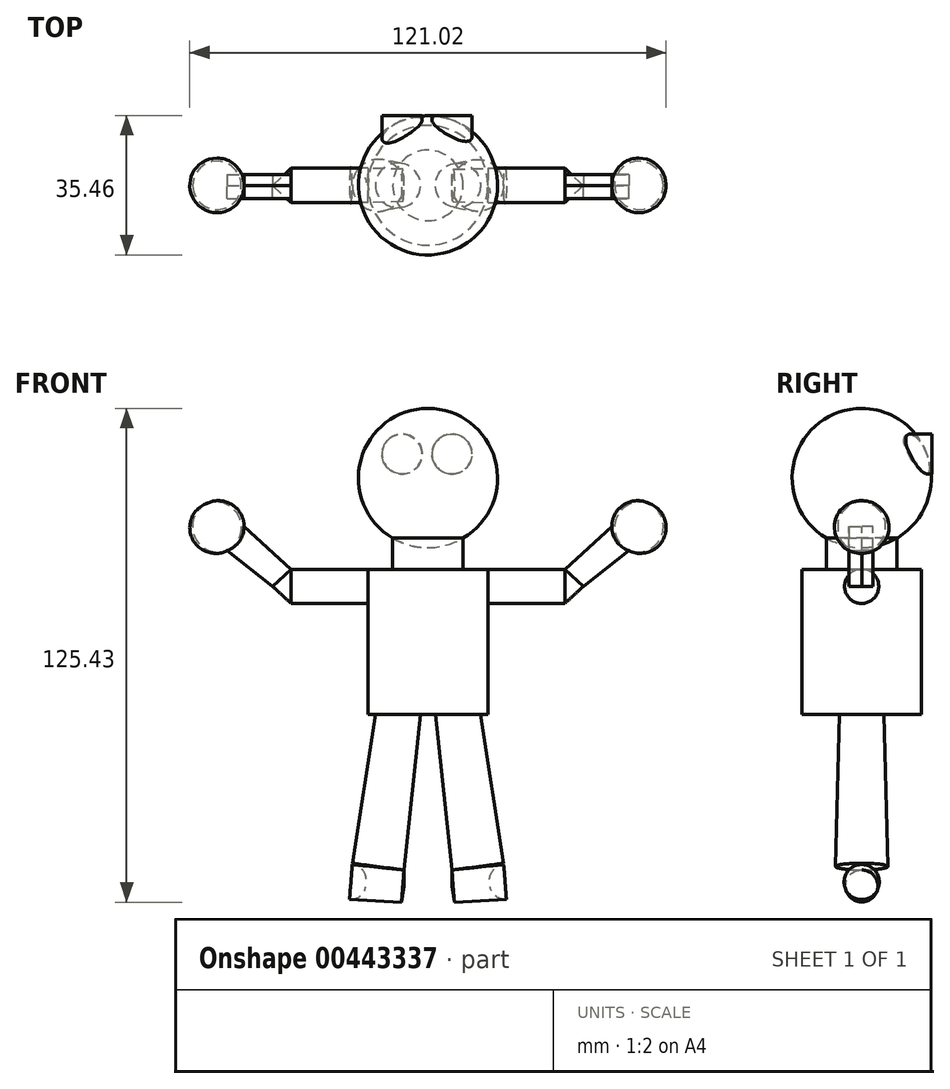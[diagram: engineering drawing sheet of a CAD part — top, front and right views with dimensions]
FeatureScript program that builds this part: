
annotation { "Feature Type Name" : "Feature", "Feature Type Description" : "" }
export const myFeature = defineFeature(function(context is Context, id is Id, definition is map)
    precondition{}
    {
        {
            var Q0;
            Q0=qCreatedBy(makeId("Front.planeOp"),FACE);
            var sketch = newSketch(context, id + "F0", { "sketchPlane" : qUnion([Q0])});
            skCircle(sketch, "E0", {"center": v(0, 44.17) * mm, "radius": 17.68 * mm});
            skLineSegment(sketch, "E1", {"start": v(-8.95, 28.92) * mm, "end": v(-8.95, 21) * mm});
            skLineSegment(sketch, "E2", {"start": v(-8.95, 21) * mm, "end": v(-22.45, 21) * mm});
            skLineSegment(sketch, "E3", {"start": v(-34.76, 21) * mm, "end": v(-46.7, 31.86) * mm});
            skLineSegment(sketch, "E4", {"start": v(0, 61.85) * mm, "end": v(0, 26.49) * mm});
            skLineSegment(sketch, "E5", {"start": v(-34.76, 21) * mm, "end": v(-22.45, 21) * mm});
            skCircle(sketch, "E6", {"center": v(-53.25, 31.87) * mm, "radius": 6.55 * mm});
            skPoint(sketch, "E6.second.point", {"position": v(-59.8, 31.86) * mm});
            skPoint(sketch, "E6.third.point", {"position": v(-56.16, 37.74) * mm});
            skLineSegment(sketch, "E7", {"start": v(-56.16, 37.74) * mm, "end": v(-51.05, 25.7) * mm});
            skLineSegment(sketch, "E8", {"start": v(-51.05, 25.7) * mm, "end": v(-39.46, 16.65) * mm});
            skLineSegment(sketch, "E9", {"start": v(-39.46, 16.65) * mm, "end": v(-33.78, 13.48) * mm});
            skLineSegment(sketch, "E10", {"start": v(-33.78, 13.48) * mm, "end": v(-15.2, 13.48) * mm});
            skLineSegment(sketch, "E11", {"start": v(-15.2, 13.48) * mm, "end": v(-15.2, -15.93) * mm});
            skLineSegment(sketch, "E12", {"start": v(-15.2, -15.93) * mm, "end": v(0, -15.93) * mm});
            skLineSegment(sketch, "E13", {"start": v(0, -15.93) * mm, "end": v(0, 61.85) * mm});
            skLineSegment(sketch, "E14", {"start": v(-8.95, 21) * mm, "end": v(0, 21) * mm});
            skLineSegment(sketch, "E15", {"start": v(-15.2, 13.48) * mm, "end": v(-15.2, 21) * mm});
            skLineSegment(sketch, "E16", {"start": v(-39.46, 16.65) * mm, "end": v(-15.2, 16.65) * mm});
            skLineSegment(sketch, "E17", {"start": v(-39.46, 16.65) * mm, "end": v(-34.76, 21) * mm});
            skCircle(sketch, "E18.MirrorC", {"center": v(53.25, 31.87) * mm, "radius": 6.55 * mm});
            skLineSegment(sketch, "E19.MirrorCS", {"start": v(34.76, 21) * mm, "end": v(46.7, 31.86) * mm});
            skLineSegment(sketch, "E20.MirrorCS", {"start": v(51.05, 25.7) * mm, "end": v(39.46, 16.65) * mm});
            skLineSegment(sketch, "E21.MirrorCS", {"start": v(39.46, 16.65) * mm, "end": v(34.76, 21) * mm});
            skLineSegment(sketch, "E22.MirrorCS", {"start": v(33.78, 13.48) * mm, "end": v(15.2, 13.48) * mm});
            skLineSegment(sketch, "E23.MirrorCS", {"start": v(39.46, 16.65) * mm, "end": v(15.2, 16.65) * mm});
            skLineSegment(sketch, "E24.MirrorCS", {"start": v(56.16, 37.74) * mm, "end": v(51.05, 25.7) * mm});
            skLineSegment(sketch, "E25", {"start": v(-12.66, -54.7) * mm, "end": v(-6.08, -55.4) * mm});
            skLineSegment(sketch, "E26", {"start": v(-6.08, -55.4) * mm, "end": v(-1.9, -15.93) * mm});
            skPoint(sketch, "E27.end.orphan", {"position": v(-12.66, -54.7) * mm});
            skPoint(sketch, "E27.start.orphan", {"position": v(-7.6, -15.93) * mm});
            skLineSegment(sketch, "E28", {"start": v(-7.6, -15.93) * mm, "end": v(-12.66, -54.7) * mm});
            skPoint(sketch, "E29.orphan", {"position": v(-19.24, -54) * mm});
            skPoint(sketch, "E30.start.orphan", {"position": v(-16.5, -58.16) * mm});
            skPoint(sketch, "E31.start.orphan", {"position": v(-6.08, -59.52) * mm});
            skPoint(sketch, "E32.end.orphan", {"position": v(-12.66, -61.61) * mm});
            skLineSegment(sketch, "E33", {"start": v(-12.66, -54.7) * mm, "end": v(-19.24, -54) * mm});
            skArc(sketch, "E34", {"start": v(-19.24, -54) * mm, "mid": v(-23.66, -58) * mm, "end": v(-19.24, -61.97) * mm});
            skLineSegment(sketch, "E35", {"start": v(-23.66, -58.16) * mm, "end": v(-6.08, -59.52) * mm});
            skLineSegment(sketch, "E36", {"start": v(-6.08, -59.52) * mm, "end": v(-6.08, -55.4) * mm});
            skSolve(sketch);
        }
        {
            var Q0;
            {var subQ0=sQuery(id+"F0.wireOp",EDGE,"E0");var subQ1=makeQuery(id+"F0.imprint","INTERSECT",VERTEX,{"derivedFrom":[subQ0,sQuery(id+"F0.wireOp",EDGE,"E1")]});Q0=makeQuery(id+"F0.imprint","IMPRINT",FACE,{"disambiguationData":[TD([[makeQuery(id+"F0.imprint","IMPRINT",EDGE,{"disambiguationData":[TD([[subQ1,1.0]])],"derivedFrom":subQ0}),1.0]])]});}
            var Q1;
            Q1=sQuery(id+"F0.wireOp",EDGE,"E4");
            revolve(context, id + "F1", {"entities" : qUnion([Q0]), "axis" : qUnion([Q1]), "revolveType" : RevolveType.FULL});
        }
        {
            var Q0;
            {var subQ0=sQuery(id+"F0.wireOp",EDGE,"E7");Q0=makeQuery(id+"F0.imprint","IMPRINT",FACE,{"disambiguationData":[TD([[makeQuery(id+"F0.imprint","IMPRINT",EDGE,{"derivedFrom":subQ0}),-1.0]])]});}
            var Q1;
            Q1=sQuery(id+"F0.wireOp",EDGE,"E7");
            revolve(context, id + "F2", {"entities" : qUnion([Q0]), "axis" : qUnion([Q1]), "revolveType" : RevolveType.FULL});
        }
        {
            var Q0;
            {var subQ3=sQuery(id+"F0.wireOp",EDGE,"E11");Q0=makeQuery(id+"F0.imprint","IMPRINT",FACE,{"disambiguationData":[TD([[makeQuery(id+"F0.imprint","IMPRINT",EDGE,{"derivedFrom":subQ3}),1.0]])]});}
            var Q1;
            Q1=sQuery(id+"F0.wireOp",EDGE,"E13");
            revolve(context, id + "F3", {"entities" : qUnion([Q0]), "axis" : qUnion([Q1]), "revolveType" : RevolveType.FULL});
        }
        {
            var Q0;
            {var subQ3=sQuery(id+"F0.wireOp",EDGE,"E16");Q0=makeQuery(id+"F0.imprint","IMPRINT",FACE,{"disambiguationData":[TD([[makeQuery(id+"F0.imprint","IMPRINT",EDGE,{"derivedFrom":subQ3}),1.0]])]});}
            var Q1;
            Q1=sQuery(id+"F0.wireOp",EDGE,"E16");
            revolve(context, id + "F4", {"entities" : qUnion([Q0]), "axis" : qUnion([Q1]), "revolveType" : RevolveType.FULL});
        }
        {
            var Q0;
            {var subQ0=sQuery(id+"F0.wireOp",EDGE,"E1");Q0=makeQuery(id+"F0.imprint","IMPRINT",FACE,{"disambiguationData":[TD([[makeQuery(id+"F0.imprint","IMPRINT",EDGE,{"derivedFrom":subQ0}),1.0]])]});}
            var Q1;
            Q1=sQuery(id+"F0.wireOp",EDGE,"E13");
            revolve(context, id + "F5", {"entities" : qUnion([Q0]), "axis" : qUnion([Q1]), "revolveType" : RevolveType.FULL});
        }
        {
            var Q0;
            Q0=makeQuery(id+"FW3MMF7VYioO6fB_0.opRevolve","SWEPT_BODY",BODY,{"disambiguationData":[OSD([sQuery(id+"F0.wireOp",EDGE,"zyPNzYHr-ha5P-rXSg-KlId-yvSlWLOifB84"),sQuery(id+"F0.wireOp",EDGE,"ewyTBzqX-5RmW-i4Gw-5EuK-rlDggEhh6qsi"),sQuery(id+"F0.wireOp",EDGE,"E5"),sQuery(id+"F0.wireOp",EDGE,"1kdRDDVu-V9N2-t5Jb-sepC-QsSfjgobqoIw")])]});
            var Q1;
            Q1=makeQuery(id+"F2.opRevolve","SWEPT_BODY",BODY,{"disambiguationData":[OSD([sQuery(id+"F0.wireOp",EDGE,"E6"),sQuery(id+"F0.wireOp",EDGE,"E7")])]});
            var Q2;
            Q2=makeQuery(id+"F4.opRevolve","SWEPT_BODY",BODY,{"disambiguationData":[OSD([sQuery(id+"F0.wireOp",EDGE,"E2"),sQuery(id+"F0.wireOp",EDGE,"E5"),sQuery(id+"F0.wireOp",EDGE,"E15"),sQuery(id+"F0.wireOp",EDGE,"E16"),sQuery(id+"F0.wireOp",EDGE,"E17")])]});
            var Q3;
            Q3=qCreatedBy(makeId("Right.planeOp"),FACE);
            mirror(context, id + "F6", {"entities" : qUnion([Q0, Q1, Q2]), "mirrorPlane" : qUnion([Q3])});
        }
        {
            var Q0;
            {var subQ0=sQuery(id+"F0.wireOp",EDGE,"E3");Q0=makeQuery(id+"F0.imprint","IMPRINT",FACE,{"disambiguationData":[TD([[makeQuery(id+"F0.imprint","IMPRINT",EDGE,{"derivedFrom":subQ0}),1.0]])]});}
            var Q1;
            {var subQ0=sQuery(id+"F0.wireOp",EDGE,"E19.MirrorCS");Q1=makeQuery(id+"F0.imprint","IMPRINT",FACE,{"disambiguationData":[TD([[makeQuery(id+"F0.imprint","IMPRINT",EDGE,{"derivedFrom":subQ0}),-1.0]])]});}
            extrude(context, id + "F7", {"entities" : qUnion([Q0, Q1]), "oppositeDirection" : true, "depth" : 2.8 * mm});
        }
        {
            var Q0;
            {var subQ0=sQuery(id+"F0.wireOp",EDGE,"E19.MirrorCS");Q0=makeQuery(id+"F0.imprint","IMPRINT",FACE,{"disambiguationData":[TD([[makeQuery(id+"F0.imprint","IMPRINT",EDGE,{"derivedFrom":subQ0}),-1.0]])]});}
            var Q1;
            {var subQ0=sQuery(id+"F0.wireOp",EDGE,"E3");Q1=makeQuery(id+"F0.imprint","IMPRINT",FACE,{"disambiguationData":[TD([[makeQuery(id+"F0.imprint","IMPRINT",EDGE,{"derivedFrom":subQ0}),1.0]])]});}
            extrude(context, id + "F8", {"entities" : qUnion([Q0, Q1]), "depth" : 3.3 * mm});
        }
        {
            var Q0;
            {var subQ0=sQuery(id+"F0.wireOp",EDGE,"E26");Q0=makeQuery(id+"F0.imprint","IMPRINT",FACE,{"disambiguationData":[TD([[makeQuery(id+"F0.imprint","IMPRINT",EDGE,{"derivedFrom":subQ0}),1.0]])]});}
            var Q1;
            Q1=sQuery(id+"F0.wireOp",EDGE,"E28");
            revolve(context, id + "F9", {"operationType" : NewBodyOperationType.ADD, "entities" : qUnion([Q0]), "axis" : qUnion([Q1]), "revolveType" : RevolveType.FULL});
        }
        {
            var Q0;
            Q0=makeQuery(id+"F3.opRevolve","SWEPT_BODY",BODY,{"disambiguationData":[OSD([sQuery(id+"F0.wireOp",EDGE,"E2"),sQuery(id+"F0.wireOp",EDGE,"E11"),sQuery(id+"F0.wireOp",EDGE,"E12"),sQuery(id+"F0.wireOp",EDGE,"E13"),sQuery(id+"F0.wireOp",EDGE,"E14"),sQuery(id+"F0.wireOp",EDGE,"E15")])]});
            var Q1;
            Q1=qCreatedBy(makeId("Right.planeOp"),FACE);
            mirror(context, id + "F10", {"entities" : qUnion([Q0]), "mirrorPlane" : qUnion([Q1])});
        }
        {
            var Q0;
            Q0=makeQuery(id+"F0.imprint","IMPRINT",FACE,{"disambiguationData":[TD([[makeQuery(id+"F0.imprint","IMPRINT",EDGE,{"derivedFrom":sQuery(id+"F0.wireOp",EDGE,"E25")}),-1.0]])]});
            var Q1;
            Q1=sQuery(id+"F0.wireOp",EDGE,"E35");
            revolve(context, id + "F11", {"operationType" : NewBodyOperationType.ADD, "entities" : qUnion([Q0]), "axis" : qUnion([Q1]), "revolveType" : RevolveType.FULL});
        }
        {
            var Q0;
            Q0=makeQuery(id+"F11.opRevolve","SWEPT_BODY",BODY,{"disambiguationData":[OSD([sQuery(id+"F0.wireOp",EDGE,"E25"),sQuery(id+"F0.wireOp",EDGE,"E33"),sQuery(id+"F0.wireOp",EDGE,"E34"),sQuery(id+"F0.wireOp",EDGE,"E35"),sQuery(id+"F0.wireOp",EDGE,"E36")])]});
            var Q1;
            Q1=qCreatedBy(makeId("Right.planeOp"),FACE);
            mirror(context, id + "F12", {"operationType" : NewBodyOperationType.ADD, "entities" : qUnion([Q0]), "mirrorPlane" : qUnion([Q1])});
        }
        {
            var Q0;
            Q0=qCreatedBy(makeId("Front.planeOp"),FACE);
            var sketch = newSketch(context, id + "F13", { "sketchPlane" : qUnion([Q0])});
            skCircle(sketch, "E37", {"center": v(-6.57, 50.26) * mm, "radius": 5.08 * mm});
            skCircle(sketch, "E38", {"center": v(6.1, 50.26) * mm, "radius": 5.08 * mm});
            skSolve(sketch);
        }
        {
            var Q0;
            Q0 = qSketchRegion(id + "F13", true);
            extrude(context, id + "F14", {"entities" : qUnion([Q0]), "operationType" : NewBodyOperationType.ADD, "oppositeDirection" : true, "depth" : 17.78 * mm});
        }
    });
